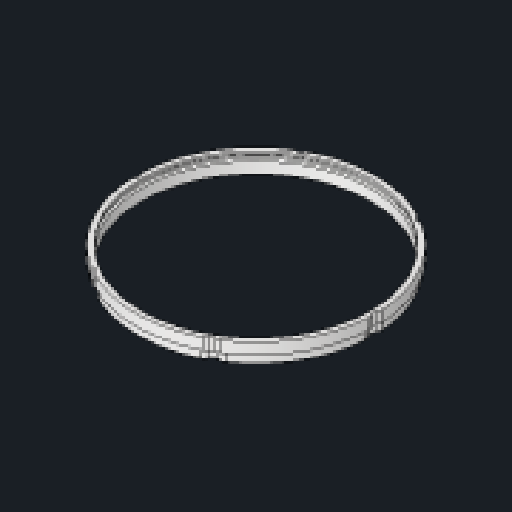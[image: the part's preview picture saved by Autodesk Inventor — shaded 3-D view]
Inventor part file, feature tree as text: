
AUTODESK INVENTOR PART (.ipt)
format: ipt  version: 2023.2 (Build 272271030, 271C)  size: 197,120 bytes
history: native  units: mm
features: sketch x3, extrude x2, revolve x1, fillet x1, pattern_circular x1
ambient origin geometry x8: Origin, YZ Plane, XZ Plane, XY Plane, X Axis, Y Axis, Z Axis, Center Point
bodies: Solid1 (feature_tree)
feature tree (8):
  revolve  "Revolution1"  [1 undecoded]
  extrude  "Extrusion1"  Depth=2.5mm
  extrude  "Extrusion2"  Depth=67.0mm
  fillet  "Fillet1"  Radius=3.5mm
  pattern_circular  "Circular Pattern1"  [2 undecoded]
  sketch  "Sketch1"  dims[d0=5.0mm d1=69.0mm]
  sketch  "Sketch2"  dims[d4=6.5mm d5=2.5mm]
  sketch  "Sketch3"  dims[d6=67.5mm d7=67.0mm d9=3.5mm d11=7.0mm d12=6.0mm d13=0.5mm d15=90.0deg d16=5.1mm d17=71.25mm d18=10.0mm d19=0.0mm d20=8.0mm d21=10.0mm d22=0.0mm d23=4.0mm d24=60.0mm d25=360.0deg d27=0.5mm d28=1.0mm]
note: 3 required parameter values undecoded (feature->parameter linkage not recoverable at this tier; creation-order binding heuristic only, values carry confidence <= 0.55)